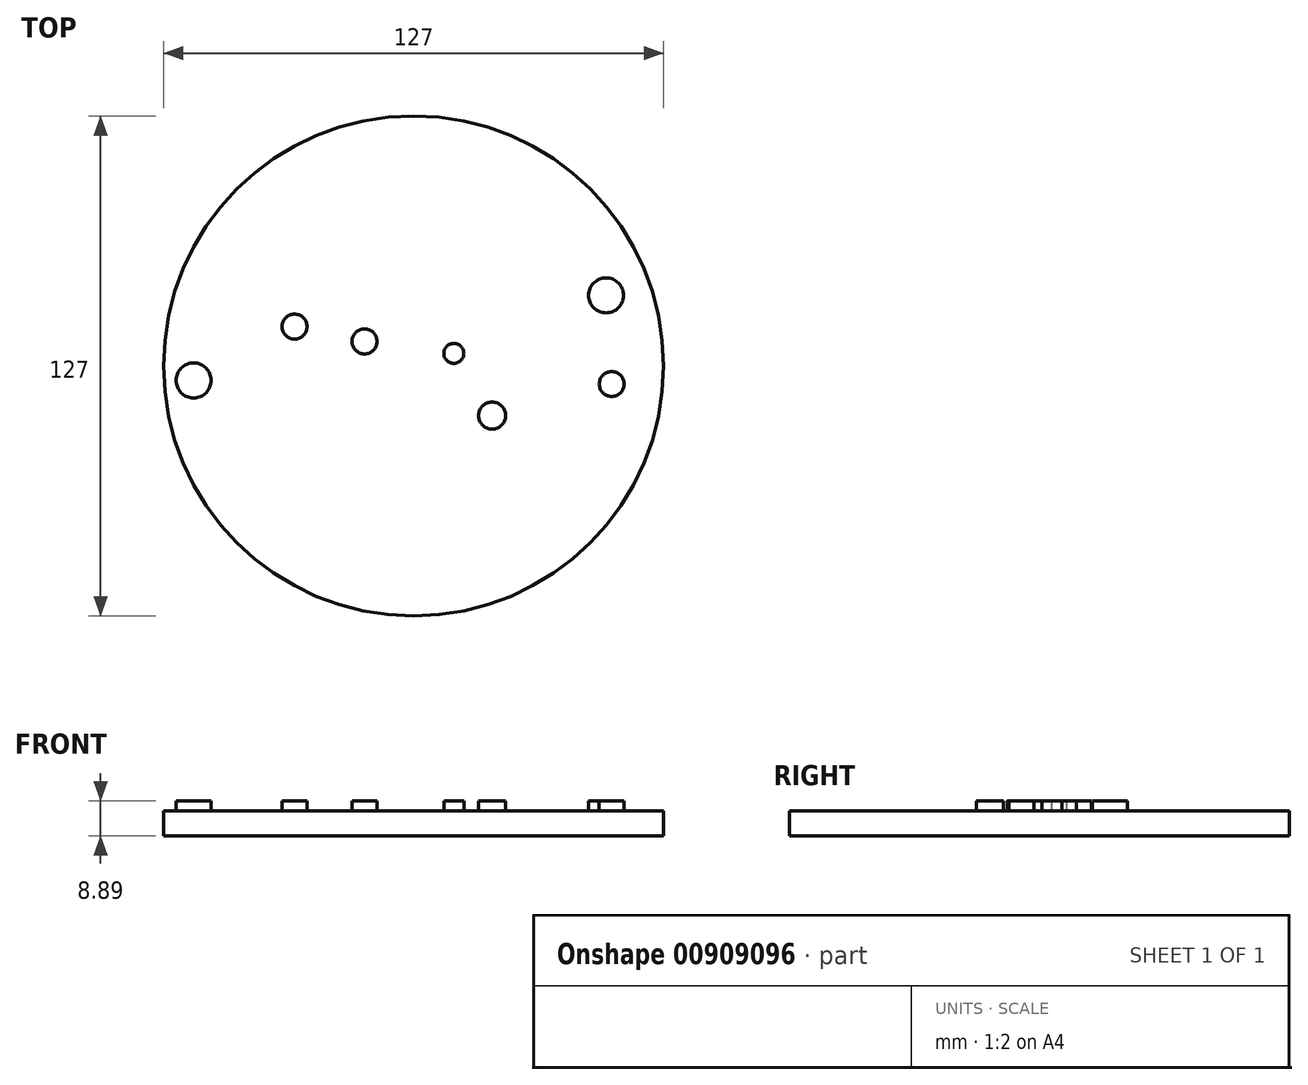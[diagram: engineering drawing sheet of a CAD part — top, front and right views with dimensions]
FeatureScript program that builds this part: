
annotation { "Feature Type Name" : "Feature", "Feature Type Description" : "" }
export const myFeature = defineFeature(function(context is Context, id is Id, definition is map)
    precondition{}
    {
        {
            var Q0;
            Q0=qCreatedBy(makeId("Top.planeOp"),FACE);
            var sketch = newSketch(context, id + "F0", { "sketchPlane" : qUnion([Q0])});
            skCircle(sketch, "E0", {"center": v(0, 0) * mm, "radius": 63.5 * mm});
            skCircle(sketch, "E1", {"center": v(-55.89, -3.67) * mm, "radius": 4.45 * mm});
            skCircle(sketch, "E2", {"center": v(-30.24, 10) * mm, "radius": 3.18 * mm});
            skCircle(sketch, "E3", {"center": v(-12.47, 6.24) * mm, "radius": 3.18 * mm});
            skCircle(sketch, "E4", {"center": v(10.23, 3.2) * mm, "radius": 2.54 * mm});
            skCircle(sketch, "E5", {"center": v(19.95, -12.61) * mm, "radius": 3.43 * mm});
            skCircle(sketch, "E6", {"center": v(50.35, -4.6) * mm, "radius": 3.18 * mm});
            skCircle(sketch, "E7", {"center": v(48.91, 17.95) * mm, "radius": 4.45 * mm});
            skSolve(sketch);
        }
        {
            var Q0;
            Q0=makeQuery(id+"F0.imprint","IMPRINT",FACE,{"disambiguationData":[TD([[makeQuery(id+"F0.imprint","IMPRINT",EDGE,{"derivedFrom":sQuery(id+"F0.wireOp",EDGE,"E0")}),1.0]])]});
            extrude(context, id + "F1", {"entities" : qUnion([Q0]), "depth" : 6.35 * mm, "offsetDistance" : 25.4 * mm});
        }
        {
            var Q0;
            Q0=makeQuery(id+"F0.imprint","IMPRINT",FACE,{"disambiguationData":[TD([[makeQuery(id+"F0.imprint","IMPRINT",EDGE,{"derivedFrom":sQuery(id+"F0.wireOp",EDGE,"E1")}),1.0]])]});
            var Q1;
            Q1=makeQuery(id+"F0.imprint","IMPRINT",FACE,{"disambiguationData":[TD([[makeQuery(id+"F0.imprint","IMPRINT",EDGE,{"derivedFrom":sQuery(id+"F0.wireOp",EDGE,"E2")}),1.0]])]});
            var Q2;
            Q2=makeQuery(id+"F0.imprint","IMPRINT",FACE,{"disambiguationData":[TD([[makeQuery(id+"F0.imprint","IMPRINT",EDGE,{"derivedFrom":sQuery(id+"F0.wireOp",EDGE,"E3")}),1.0]])]});
            var Q3;
            Q3=makeQuery(id+"F0.imprint","IMPRINT",FACE,{"disambiguationData":[TD([[makeQuery(id+"F0.imprint","IMPRINT",EDGE,{"derivedFrom":sQuery(id+"F0.wireOp",EDGE,"E4")}),1.0]])]});
            var Q4;
            Q4=makeQuery(id+"F0.imprint","IMPRINT",FACE,{"disambiguationData":[TD([[makeQuery(id+"F0.imprint","IMPRINT",EDGE,{"derivedFrom":sQuery(id+"F0.wireOp",EDGE,"E7")}),1.0]])]});
            var Q5;
            Q5=makeQuery(id+"F0.imprint","IMPRINT",FACE,{"disambiguationData":[TD([[makeQuery(id+"F0.imprint","IMPRINT",EDGE,{"derivedFrom":sQuery(id+"F0.wireOp",EDGE,"E6")}),1.0]])]});
            var Q6;
            Q6=makeQuery(id+"F0.imprint","IMPRINT",FACE,{"disambiguationData":[TD([[makeQuery(id+"F0.imprint","IMPRINT",EDGE,{"derivedFrom":sQuery(id+"F0.wireOp",EDGE,"E5")}),1.0]])]});
            extrude(context, id + "F2", {"entities" : qUnion([Q0, Q1, Q2, Q3, Q4, Q5, Q6]), "operationType" : NewBodyOperationType.ADD, "depth" : 8.9 * mm, "offsetDistance" : 25.4 * mm});
        }
    });
